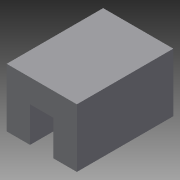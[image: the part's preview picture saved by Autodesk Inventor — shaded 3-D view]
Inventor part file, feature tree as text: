
AUTODESK INVENTOR PART (.ipt)
format: ipt  version: 2015 (Build 190159000, 159)  size: 84,480 bytes
history: native  units: mm
features: extrude x2, sketch x2
ambient origin geometry x8: Origin, YZ Plane, XZ Plane, XY Plane, X Axis, Y Axis, Z Axis, Center Point
bodies: Solid1 (feature_tree)
feature tree (4):
  extrude  "Extrusion1"  Depth=2.0mm
  extrude  "Extrusion2"  Depth=5.0mm TaperAngle=0.0deg
  sketch  "Sketch1"  dims[d0=6.0mm d1=2.0mm]
  sketch  "Sketch2"  dims[d2=2.0mm d3=5.0mm d4=0.0mm d5=2.0mm d6=0.0mm]
